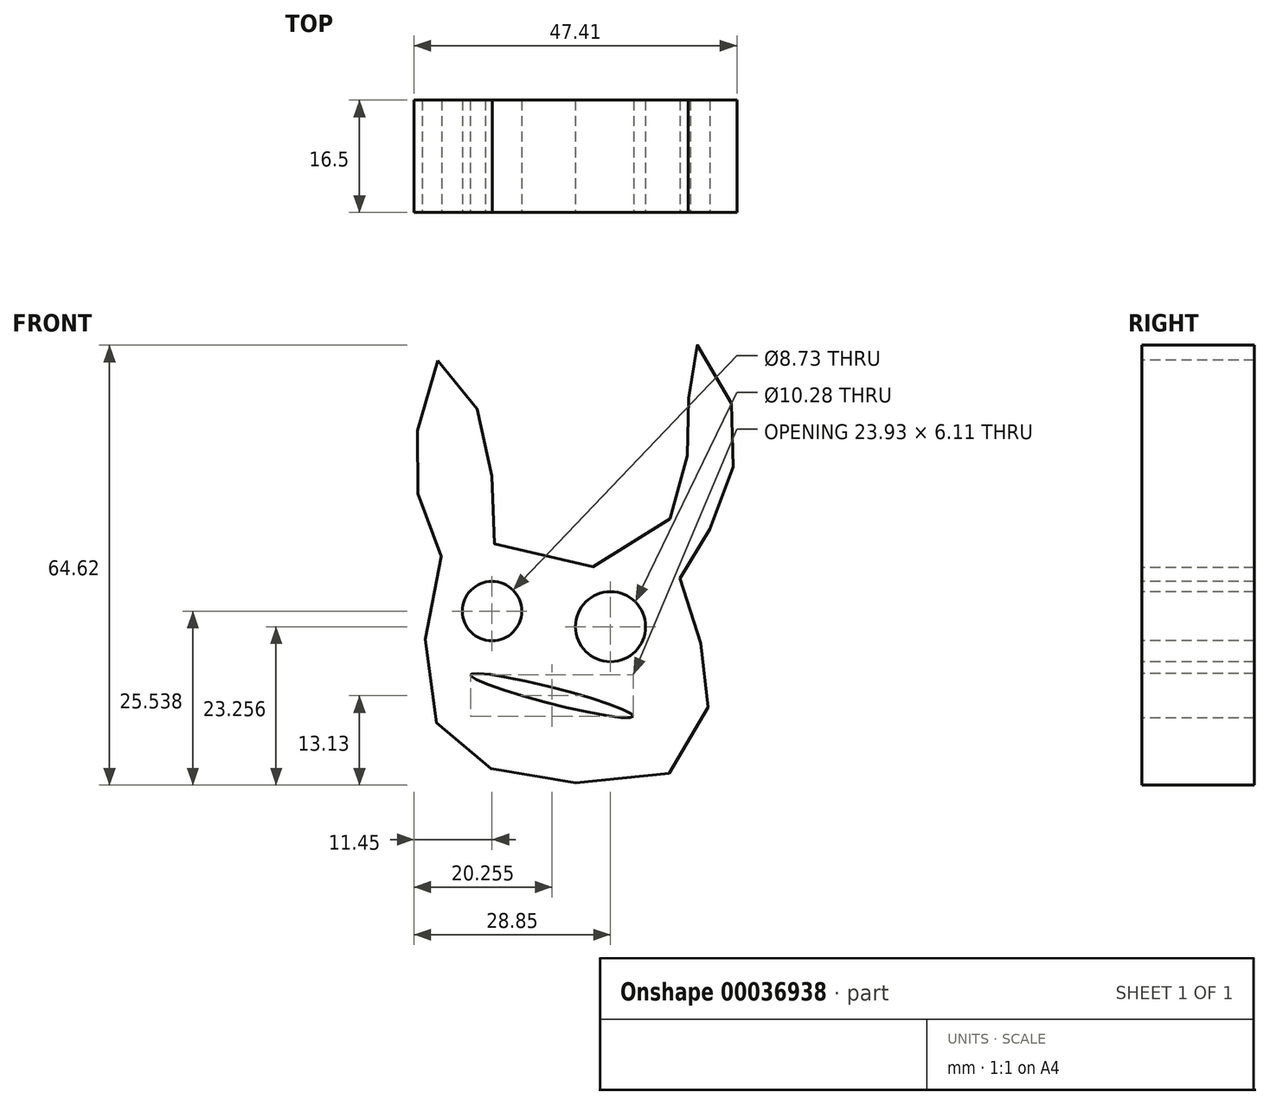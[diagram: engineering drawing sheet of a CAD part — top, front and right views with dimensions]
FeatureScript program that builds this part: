
annotation { "Feature Type Name" : "Feature", "Feature Type Description" : "" }
export const myFeature = defineFeature(function(context is Context, id is Id, definition is map)
    precondition{}
    {
        {
            var Q0;
            Q0=qCreatedBy(makeId("Front.planeOp"),FACE);
            var sketch = newSketch(context, id + "F0", { "sketchPlane" : qUnion([Q0])});
            skFitSpline(sketch, "E0", {"points": [v(-43.36, 49.2) * mm, v(-46.5, 37.5) * mm, v(-46.2, 29.52) * mm, v(-42.79, 20.1) * mm, v(-45.64, 4.14) * mm, v(-39.93, -8.41) * mm, v(-28.52, -12.12) * mm, v(-9.13, -11.27) * mm, v(-3.42, 0) * mm, v(-5.13, 8.7) * mm, v(-7.7, 18.11) * mm, v(-3.42, 24.39) * mm, v(0, 33.52) * mm, v(0, 42.07) * mm, v(-5.13, 51.49) * mm, v(-6.56, 47.5) * mm, v(-6.28, 37.8) * mm, v(-7.42, 32.66) * mm, v(-13.4, 20.97) * mm, v(-35.08, 22.4) * mm, v(-35.37, 32.66) * mm, v(-37.94, 42.93) * mm, v(-43.36, 49.2) * mm]});
            skCircle(sketch, "E1", {"center": v(-35.37, 12.4) * mm, "radius": 4.36 * mm});
            skCircle(sketch, "E2", {"center": v(-17.97, 10.13) * mm, "radius": 5.14 * mm});
            skEllipse(sketch, "E3", {"center": v(-26.56, 0) * mm, "majorRadius": 12.35 * mm, "minorRadius": 1.19 * mm, "majorAxis": v(0.97, -0.25)});
            skSolve(sketch);
        }
        {
            var Q0;
            Q0=makeQuery(id+"F0.imprint","IMPRINT",FACE,{"disambiguationData":[TD([[makeQuery(id+"F0.imprint","IMPRINT",EDGE,{"derivedFrom":sQuery(id+"F0.wireOp",EDGE,"E0")}),1.0]])]});
            extrude(context, id + "F1", {"entities" : qUnion([Q0]), "oppositeDirection" : true, "depth" : 16.5 * mm});
        }
    });
